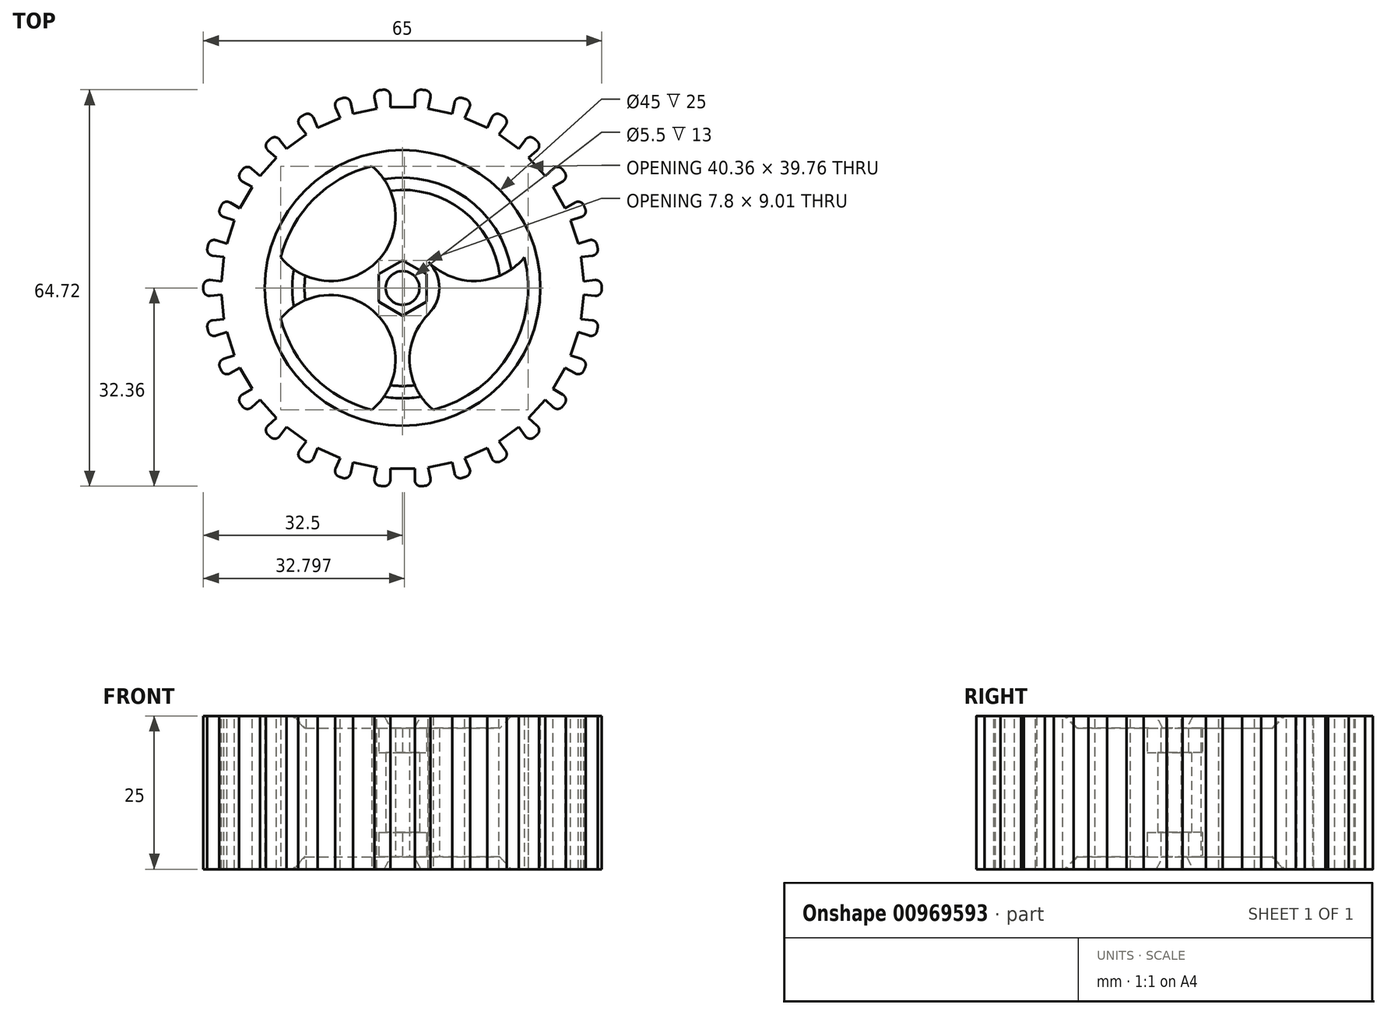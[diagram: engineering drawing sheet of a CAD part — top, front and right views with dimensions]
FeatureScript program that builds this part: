
annotation { "Feature Type Name" : "Feature", "Feature Type Description" : "" }
export const myFeature = defineFeature(function(context is Context, id is Id, definition is map)
    precondition{}
    {
        {
            var Q0;
            Q0=qCreatedBy(makeId("Top.planeOp"),FACE);
            var sketch = newSketch(context, id + "F0", { "sketchPlane" : qUnion([Q0])});
            skCircle(sketch, "E0", {"center": v(0, 0) * mm, "radius": 32.5 * mm});
            skCircle(sketch, "E1", {"center": v(0, 0) * mm, "radius": 22.5 * mm});
            skCircle(sketch, "E2", {"center": v(0, 0) * mm, "radius": 23.5 * mm});
            skCircle(sketch, "E3", {"center": v(0, 0) * mm, "radius": 20.5 * mm});
            skCircle(sketch, "E4", {"center": v(0, 0) * mm, "radius": 6 * mm});
            skArc(sketch, "E5", {"start": v(-19.88, 5) * mm, "mid": v(-4.24, 4.24) * mm, "end": v(-5, 19.88) * mm});
            skArc(sketch, "E6.MirrorCS", {"start": v(19.88, 5) * mm, "mid": v(4.24, 4.24) * mm, "end": v(5, 19.88) * mm});
            skArc(sketch, "E7.MirrorCS", {"start": v(-19.88, -5) * mm, "mid": v(-4.24, -4.24) * mm, "end": v(-5, -19.88) * mm});
            skArc(sketch, "E8.MirrorCS", {"start": v(19.88, -5) * mm, "mid": v(4.24, -4.24) * mm, "end": v(5, -19.88) * mm});
            skCircle(sketch, "E9.cCircle", {"center": v(0, 0) * mm, "radius": 3.9 * mm, "construction": true});
            skLineSegment(sketch, "E9.0", {"start": v(3.9, 2.25) * mm, "end": v(3.9, -2.25) * mm});
            skLineSegment(sketch, "E9.1", {"start": v(3.9, -2.25) * mm, "end": v(0, -4.5) * mm});
            skLineSegment(sketch, "E9.2", {"start": v(0, -4.5) * mm, "end": v(-3.9, -2.25) * mm});
            skLineSegment(sketch, "E9.3", {"start": v(-3.9, -2.25) * mm, "end": v(-3.9, 2.25) * mm});
            skLineSegment(sketch, "E9.4", {"start": v(-3.9, 2.25) * mm, "end": v(0, 4.5) * mm});
            skLineSegment(sketch, "E9.5", {"start": v(0, 4.5) * mm, "end": v(3.9, 2.25) * mm});
            skPoint(sketch, "E9.0.midPoint", {"position": v(3.9, 0) * mm});
            skCircle(sketch, "E10", {"center": v(0, 0) * mm, "radius": 3 * mm});
            skCircle(sketch, "E11", {"center": v(0, 0) * mm, "radius": 2.75 * mm});
            skSolve(sketch);
        }
        {
            var Q0;
            {var subQ0=sQuery(id+"F0.wireOp",EDGE,"E5");var subQ1=sQuery(id+"F0.wireOp",EDGE,"E3");var subQ2=makeQuery(id+"F0.imprint","INTERSECT",VERTEX,{"disambiguationData":[OD(1.0)],"derivedFrom":[subQ1,subQ0]});Q0=makeQuery(id+"F0.imprint","IMPRINT",FACE,{"disambiguationData":[TD([[makeQuery(id+"F0.imprint","IMPRINT",EDGE,{"disambiguationData":[TD([[subQ2,1.0]])],"derivedFrom":subQ1}),1.0]])]});}
            var Q1;
            {var subQ0=sQuery(id+"F0.wireOp",EDGE,"E5");var subQ1=sQuery(id+"F0.wireOp",EDGE,"E3");var subQ2=makeQuery(id+"F0.imprint","INTERSECT",VERTEX,{"disambiguationData":[OD(0.0)],"derivedFrom":[subQ1,subQ0]});Q1=makeQuery(id+"F0.imprint","IMPRINT",FACE,{"disambiguationData":[TD([[makeQuery(id+"F0.imprint","IMPRINT",EDGE,{"disambiguationData":[TD([[subQ2,-1.0]])],"derivedFrom":subQ1}),1.0]])]});}
            var Q2;
            {var subQ0=sQuery(id+"F0.wireOp",EDGE,"E7.MirrorCS");var subQ1=sQuery(id+"F0.wireOp",EDGE,"E3");var subQ2=makeQuery(id+"F0.imprint","INTERSECT",VERTEX,{"disambiguationData":[OD(1.0)],"derivedFrom":[subQ1,subQ0]});Q2=makeQuery(id+"F0.imprint","IMPRINT",FACE,{"disambiguationData":[TD([[makeQuery(id+"F0.imprint","IMPRINT",EDGE,{"disambiguationData":[TD([[subQ2,-1.0]])],"derivedFrom":subQ1}),1.0]])]});}
            var Q3;
            {var subQ0=sQuery(id+"F0.wireOp",EDGE,"E6.MirrorCS");var subQ1=sQuery(id+"F0.wireOp",EDGE,"E3");var subQ2=makeQuery(id+"F0.imprint","INTERSECT",VERTEX,{"disambiguationData":[OD(0.0)],"derivedFrom":[subQ1,subQ0]});Q3=makeQuery(id+"F0.imprint","IMPRINT",FACE,{"disambiguationData":[TD([[makeQuery(id+"F0.imprint","IMPRINT",EDGE,{"disambiguationData":[TD([[subQ2,1.0]])],"derivedFrom":subQ1}),1.0]])]});}
            var Q4;
            Q4=makeQuery(id+"F0.imprint","IMPRINT",FACE,{"disambiguationData":[TD([[makeQuery(id+"F0.imprint","IMPRINT",EDGE,{"derivedFrom":sQuery(id+"F0.wireOp",EDGE,"E1")}),1.0]])]});
            var Q5;
            Q5=makeQuery(id+"F0.imprint","IMPRINT",FACE,{"disambiguationData":[TD([[makeQuery(id+"F0.imprint","IMPRINT",EDGE,{"derivedFrom":sQuery(id+"F0.wireOp",EDGE,"E9.0")}),1.0]])]});
            var Q6;
            Q6=makeQuery(id+"F0.imprint","IMPRINT",FACE,{"disambiguationData":[TD([[makeQuery(id+"F0.imprint","IMPRINT",EDGE,{"derivedFrom":sQuery(id+"F0.wireOp",EDGE,"E9.0")}),-1.0]])]});
            extrude(context, id + "F1", {"entities" : qUnion([Q0, Q1, Q2, Q3, Q4, Q5, Q6]), "depth" : 25 * mm, "offsetDistance" : 25 * mm});
        }
        {
            var Q0;
            Q0=makeQuery(id+"F0.imprint","IMPRINT",FACE,{"disambiguationData":[TD([[makeQuery(id+"F0.imprint","IMPRINT",EDGE,{"derivedFrom":sQuery(id+"F0.wireOp",EDGE,"E0")}),1.0]])]});
            var Q1;
            Q1=makeQuery(id+"F0.imprint","IMPRINT",FACE,{"disambiguationData":[TD([[makeQuery(id+"F0.imprint","IMPRINT",EDGE,{"derivedFrom":sQuery(id+"F0.wireOp",EDGE,"E1")}),-1.0]])]});
            extrude(context, id + "F2", {"entities" : qUnion([Q0, Q1]), "depth" : 25 * mm, "offsetDistance" : 25 * mm});
        }
        {
            var Q0;
            Q0=makeQuery(id+"F0.imprint","IMPRINT",FACE,{"disambiguationData":[TD([[makeQuery(id+"F0.imprint","IMPRINT",EDGE,{"derivedFrom":sQuery(id+"F0.wireOp",EDGE,"E10")}),1.0]])]});
            extrude(context, id + "F3", {"entities" : qUnion([Q0]), "operationType" : NewBodyOperationType.ADD, "depth" : 23 * mm, "offsetDistance" : 25 * mm, "hasSecondDirection" : true, "secondDirectionOppositeDirection" : true, "secondDirectionDepth" : -2 * mm});
        }
        {
            var Q0;
            Q0=makeQuery(id+"F1.opExtrude","CAP_EDGE",EDGE,{"disambiguationData":[OSD([sQuery(id+"F0.wireOp",EDGE,"E10")])],"isStart":true});
            var Q1;
            Q1=makeQuery(id+"F1.opExtrude","CAP_EDGE",EDGE,{"disambiguationData":[OSD([sQuery(id+"F0.wireOp",EDGE,"E10")])],"isStart":false});
            chamfer(context, id + "F4", {"entities" : qUnion([Q0, Q1]), "width" : 15 * mm, "tangentPropagation" : true});
        }
        {
            var Q0;
            Q0=qCreatedBy(makeId("Front.planeOp"),FACE);
            cPlane(context, id + "F5", {"entities" : qUnion([Q0]), "cplaneType" : CPlaneType.OFFSET, "offset" : 32.5 * mm, "width" : 150 * mm, "height" : 150 * mm});
        }
        {
            var Q0;
            Q0=qCreatedBy(id+"F5.planeOp",FACE);
            var sketch = newSketch(context, id + "F6", { "sketchPlane" : qUnion([Q0])});
            skLineSegment(sketch, "E12.bottom", {"start": v(-2, 0) * mm, "end": v(2, 0) * mm});
            skLineSegment(sketch, "E12.top", {"start": v(-2, 25) * mm, "end": v(2, 25) * mm});
            skLineSegment(sketch, "E12.left", {"start": v(-2, 0) * mm, "end": v(-2, 25) * mm});
            skLineSegment(sketch, "E12.right", {"start": v(2, 0) * mm, "end": v(2, 25) * mm});
            skSolve(sketch);
        }
        {
            var Q0;
            Q0=makeQuery(id+"F6.imprint","IMPRINT",FACE,{"disambiguationData":[TD([[makeQuery(id+"F6.imprint","IMPRINT",EDGE,{"derivedFrom":sQuery(id+"F6.wireOp",EDGE,"E12.bottom")}),1.0]])]});
            extrude(context, id + "F7", {"entities" : qUnion([Q0]), "oppositeDirection" : true, "depth" : 3 * mm, "offsetDistance" : 25 * mm});
        }
        {
            var Q0;
            Q0=makeQuery(id+"F7.opExtrude","SWEPT_BODY",BODY,{"disambiguationData":[OSD([sQuery(id+"F6.wireOp",EDGE,"E12.bottom"),sQuery(id+"F6.wireOp",EDGE,"E12.top"),sQuery(id+"F6.wireOp",EDGE,"E12.left"),sQuery(id+"F6.wireOp",EDGE,"E12.right")])]});
            var Q1;
            Q1=makeQuery(id+"F3.opExtrude","CAP_EDGE",EDGE,{"disambiguationData":[OSD([sQuery(id+"F0.wireOp",EDGE,"E11")])],"isStart":false});
            circularPattern(context, id + "F8", {"operationType" : NewBodyOperationType.REMOVE, "entities" : qUnion([Q0]), "axis" : qUnion([Q1]), "angle" : 360 * degree, "instanceCount" : 30, "equalSpace" : true});
        }
        {
            var Q0;
            Q0=makeQuery(id+"F0.imprint","IMPRINT",FACE,{"disambiguationData":[TD([[makeQuery(id+"F0.imprint","IMPRINT",EDGE,{"derivedFrom":sQuery(id+"F0.wireOp",EDGE,"E10")}),1.0]])]});
            var Q1;
            Q1=makeQuery(id+"F0.imprint","IMPRINT",FACE,{"disambiguationData":[TD([[makeQuery(id+"F0.imprint","IMPRINT",EDGE,{"derivedFrom":sQuery(id+"F0.wireOp",EDGE,"E9.0")}),-1.0]])]});
            extrude(context, id + "F9", {"entities" : qUnion([Q0, Q1]), "operationType" : NewBodyOperationType.REMOVE, "depth" : 6 * mm, "offsetDistance" : 25 * mm});
        }
        {
            var Q0;
            Q0=makeQuery(id+"F0.imprint","IMPRINT",FACE,{"disambiguationData":[TD([[makeQuery(id+"F0.imprint","IMPRINT",EDGE,{"derivedFrom":sQuery(id+"F0.wireOp",EDGE,"E9.0")}),-1.0]])]});
            var Q1;
            Q1=makeQuery(id+"F0.imprint","IMPRINT",FACE,{"disambiguationData":[TD([[makeQuery(id+"F0.imprint","IMPRINT",EDGE,{"derivedFrom":sQuery(id+"F0.wireOp",EDGE,"E10")}),1.0]])]});
            extrude(context, id + "F10", {"entities" : qUnion([Q0, Q1]), "operationType" : NewBodyOperationType.REMOVE, "depth" : 25 * mm, "offsetDistance" : 25 * mm, "hasSecondDirection" : true, "secondDirectionOppositeDirection" : false, "secondDirectionDepth" : 19 * mm});
        }
        {
            var Q0;
            Q0=makeQuery(id+"F8.boolean.opBoolean","INTERSECT",EDGE,{"derivedFrom":[makeQuery(id+"F2.opExtrude","SWEPT_FACE",FACE,{"disambiguationData":[OSD([sQuery(id+"F0.wireOp",EDGE,"E0")])]}),makeQuery(id+"F8.opPattern","COPY",FACE,{"derivedFrom":makeQuery(id+"F7.opExtrude","SWEPT_FACE",FACE,{"disambiguationData":[OSD([sQuery(id+"F6.wireOp",EDGE,"E12.right")])]}),"instanceName":"17"})]});
            var Q1;
            Q1=makeQuery(id+"F8.boolean.opBoolean","INTERSECT",EDGE,{"derivedFrom":[makeQuery(id+"F2.opExtrude","SWEPT_FACE",FACE,{"disambiguationData":[OSD([sQuery(id+"F0.wireOp",EDGE,"E0")])]}),makeQuery(id+"F8.opPattern","COPY",FACE,{"derivedFrom":makeQuery(id+"F7.opExtrude","SWEPT_FACE",FACE,{"disambiguationData":[OSD([sQuery(id+"F6.wireOp",EDGE,"E12.left")])]}),"instanceName":"18"})]});
            var Q2;
            Q2=makeQuery(id+"F8.boolean.opBoolean","INTERSECT",EDGE,{"derivedFrom":[makeQuery(id+"F2.opExtrude","SWEPT_FACE",FACE,{"disambiguationData":[OSD([sQuery(id+"F0.wireOp",EDGE,"E0")])]}),makeQuery(id+"F8.opPattern","COPY",FACE,{"derivedFrom":makeQuery(id+"F7.opExtrude","SWEPT_FACE",FACE,{"disambiguationData":[OSD([sQuery(id+"F6.wireOp",EDGE,"E12.right")])]}),"instanceName":"18"})]});
            var Q3;
            Q3=makeQuery(id+"F8.boolean.opBoolean","INTERSECT",EDGE,{"derivedFrom":[makeQuery(id+"F2.opExtrude","SWEPT_FACE",FACE,{"disambiguationData":[OSD([sQuery(id+"F0.wireOp",EDGE,"E0")])]}),makeQuery(id+"F8.opPattern","COPY",FACE,{"derivedFrom":makeQuery(id+"F7.opExtrude","SWEPT_FACE",FACE,{"disambiguationData":[OSD([sQuery(id+"F6.wireOp",EDGE,"E12.left")])]}),"instanceName":"19"})]});
            var Q4;
            Q4=makeQuery(id+"F8.boolean.opBoolean","INTERSECT",EDGE,{"derivedFrom":[makeQuery(id+"F2.opExtrude","SWEPT_FACE",FACE,{"disambiguationData":[OSD([sQuery(id+"F0.wireOp",EDGE,"E0")])]}),makeQuery(id+"F8.opPattern","COPY",FACE,{"derivedFrom":makeQuery(id+"F7.opExtrude","SWEPT_FACE",FACE,{"disambiguationData":[OSD([sQuery(id+"F6.wireOp",EDGE,"E12.right")])]}),"instanceName":"19"})]});
            var Q5;
            Q5=makeQuery(id+"F8.boolean.opBoolean","INTERSECT",EDGE,{"derivedFrom":[makeQuery(id+"F2.opExtrude","SWEPT_FACE",FACE,{"disambiguationData":[OSD([sQuery(id+"F0.wireOp",EDGE,"E0")])]}),makeQuery(id+"F8.opPattern","COPY",FACE,{"derivedFrom":makeQuery(id+"F7.opExtrude","SWEPT_FACE",FACE,{"disambiguationData":[OSD([sQuery(id+"F6.wireOp",EDGE,"E12.left")])]}),"instanceName":"20"})]});
            var Q6;
            Q6=makeQuery(id+"F8.boolean.opBoolean","INTERSECT",EDGE,{"derivedFrom":[makeQuery(id+"F2.opExtrude","SWEPT_FACE",FACE,{"disambiguationData":[OSD([sQuery(id+"F0.wireOp",EDGE,"E0")])]}),makeQuery(id+"F8.opPattern","COPY",FACE,{"derivedFrom":makeQuery(id+"F7.opExtrude","SWEPT_FACE",FACE,{"disambiguationData":[OSD([sQuery(id+"F6.wireOp",EDGE,"E12.right")])]}),"instanceName":"20"})]});
            var Q7;
            Q7=makeQuery(id+"F8.boolean.opBoolean","INTERSECT",EDGE,{"derivedFrom":[makeQuery(id+"F2.opExtrude","SWEPT_FACE",FACE,{"disambiguationData":[OSD([sQuery(id+"F0.wireOp",EDGE,"E0")])]}),makeQuery(id+"F8.opPattern","COPY",FACE,{"derivedFrom":makeQuery(id+"F7.opExtrude","SWEPT_FACE",FACE,{"disambiguationData":[OSD([sQuery(id+"F6.wireOp",EDGE,"E12.left")])]}),"instanceName":"21"})]});
            var Q8;
            Q8=makeQuery(id+"F8.boolean.opBoolean","INTERSECT",EDGE,{"derivedFrom":[makeQuery(id+"F2.opExtrude","SWEPT_FACE",FACE,{"disambiguationData":[OSD([sQuery(id+"F0.wireOp",EDGE,"E0")])]}),makeQuery(id+"F8.opPattern","COPY",FACE,{"derivedFrom":makeQuery(id+"F7.opExtrude","SWEPT_FACE",FACE,{"disambiguationData":[OSD([sQuery(id+"F6.wireOp",EDGE,"E12.right")])]}),"instanceName":"21"})]});
            var Q9;
            Q9=makeQuery(id+"F8.boolean.opBoolean","INTERSECT",EDGE,{"derivedFrom":[makeQuery(id+"F2.opExtrude","SWEPT_FACE",FACE,{"disambiguationData":[OSD([sQuery(id+"F0.wireOp",EDGE,"E0")])]}),makeQuery(id+"F8.opPattern","COPY",FACE,{"derivedFrom":makeQuery(id+"F7.opExtrude","SWEPT_FACE",FACE,{"disambiguationData":[OSD([sQuery(id+"F6.wireOp",EDGE,"E12.left")])]}),"instanceName":"22"})]});
            var Q10;
            Q10=makeQuery(id+"F8.boolean.opBoolean","INTERSECT",EDGE,{"derivedFrom":[makeQuery(id+"F2.opExtrude","SWEPT_FACE",FACE,{"disambiguationData":[OSD([sQuery(id+"F0.wireOp",EDGE,"E0")])]}),makeQuery(id+"F8.opPattern","COPY",FACE,{"derivedFrom":makeQuery(id+"F7.opExtrude","SWEPT_FACE",FACE,{"disambiguationData":[OSD([sQuery(id+"F6.wireOp",EDGE,"E12.right")])]}),"instanceName":"22"})]});
            var Q11;
            Q11=makeQuery(id+"F8.boolean.opBoolean","INTERSECT",EDGE,{"derivedFrom":[makeQuery(id+"F2.opExtrude","SWEPT_FACE",FACE,{"disambiguationData":[OSD([sQuery(id+"F0.wireOp",EDGE,"E0")])]}),makeQuery(id+"F8.opPattern","COPY",FACE,{"derivedFrom":makeQuery(id+"F7.opExtrude","SWEPT_FACE",FACE,{"disambiguationData":[OSD([sQuery(id+"F6.wireOp",EDGE,"E12.left")])]}),"instanceName":"23"})]});
            var Q12;
            Q12=makeQuery(id+"F8.boolean.opBoolean","INTERSECT",EDGE,{"derivedFrom":[makeQuery(id+"F2.opExtrude","SWEPT_FACE",FACE,{"disambiguationData":[OSD([sQuery(id+"F0.wireOp",EDGE,"E0")])]}),makeQuery(id+"F8.opPattern","COPY",FACE,{"derivedFrom":makeQuery(id+"F7.opExtrude","SWEPT_FACE",FACE,{"disambiguationData":[OSD([sQuery(id+"F6.wireOp",EDGE,"E12.right")])]}),"instanceName":"23"})]});
            var Q13;
            Q13=makeQuery(id+"F8.boolean.opBoolean","INTERSECT",EDGE,{"derivedFrom":[makeQuery(id+"F2.opExtrude","SWEPT_FACE",FACE,{"disambiguationData":[OSD([sQuery(id+"F0.wireOp",EDGE,"E0")])]}),makeQuery(id+"F8.opPattern","COPY",FACE,{"derivedFrom":makeQuery(id+"F7.opExtrude","SWEPT_FACE",FACE,{"disambiguationData":[OSD([sQuery(id+"F6.wireOp",EDGE,"E12.left")])]}),"instanceName":"24"})]});
            var Q14;
            Q14=makeQuery(id+"F8.boolean.opBoolean","INTERSECT",EDGE,{"derivedFrom":[makeQuery(id+"F2.opExtrude","SWEPT_FACE",FACE,{"disambiguationData":[OSD([sQuery(id+"F0.wireOp",EDGE,"E0")])]}),makeQuery(id+"F8.opPattern","COPY",FACE,{"derivedFrom":makeQuery(id+"F7.opExtrude","SWEPT_FACE",FACE,{"disambiguationData":[OSD([sQuery(id+"F6.wireOp",EDGE,"E12.right")])]}),"instanceName":"24"})]});
            var Q15;
            Q15=makeQuery(id+"F8.boolean.opBoolean","INTERSECT",EDGE,{"derivedFrom":[makeQuery(id+"F2.opExtrude","SWEPT_FACE",FACE,{"disambiguationData":[OSD([sQuery(id+"F0.wireOp",EDGE,"E0")])]}),makeQuery(id+"F8.opPattern","COPY",FACE,{"derivedFrom":makeQuery(id+"F7.opExtrude","SWEPT_FACE",FACE,{"disambiguationData":[OSD([sQuery(id+"F6.wireOp",EDGE,"E12.left")])]}),"instanceName":"25"})]});
            var Q16;
            Q16=makeQuery(id+"F8.boolean.opBoolean","INTERSECT",EDGE,{"derivedFrom":[makeQuery(id+"F2.opExtrude","SWEPT_FACE",FACE,{"disambiguationData":[OSD([sQuery(id+"F0.wireOp",EDGE,"E0")])]}),makeQuery(id+"F8.opPattern","COPY",FACE,{"derivedFrom":makeQuery(id+"F7.opExtrude","SWEPT_FACE",FACE,{"disambiguationData":[OSD([sQuery(id+"F6.wireOp",EDGE,"E12.right")])]}),"instanceName":"25"})]});
            var Q17;
            Q17=makeQuery(id+"F8.boolean.opBoolean","INTERSECT",EDGE,{"derivedFrom":[makeQuery(id+"F2.opExtrude","SWEPT_FACE",FACE,{"disambiguationData":[OSD([sQuery(id+"F0.wireOp",EDGE,"E0")])]}),makeQuery(id+"F8.opPattern","COPY",FACE,{"derivedFrom":makeQuery(id+"F7.opExtrude","SWEPT_FACE",FACE,{"disambiguationData":[OSD([sQuery(id+"F6.wireOp",EDGE,"E12.left")])]}),"instanceName":"26"})]});
            var Q18;
            Q18=makeQuery(id+"F8.boolean.opBoolean","INTERSECT",EDGE,{"derivedFrom":[makeQuery(id+"F2.opExtrude","SWEPT_FACE",FACE,{"disambiguationData":[OSD([sQuery(id+"F0.wireOp",EDGE,"E0")])]}),makeQuery(id+"F8.opPattern","COPY",FACE,{"derivedFrom":makeQuery(id+"F7.opExtrude","SWEPT_FACE",FACE,{"disambiguationData":[OSD([sQuery(id+"F6.wireOp",EDGE,"E12.right")])]}),"instanceName":"26"})]});
            var Q19;
            Q19=makeQuery(id+"F8.boolean.opBoolean","INTERSECT",EDGE,{"derivedFrom":[makeQuery(id+"F2.opExtrude","SWEPT_FACE",FACE,{"disambiguationData":[OSD([sQuery(id+"F0.wireOp",EDGE,"E0")])]}),makeQuery(id+"F8.opPattern","COPY",FACE,{"derivedFrom":makeQuery(id+"F7.opExtrude","SWEPT_FACE",FACE,{"disambiguationData":[OSD([sQuery(id+"F6.wireOp",EDGE,"E12.left")])]}),"instanceName":"27"})]});
            var Q20;
            Q20=makeQuery(id+"F8.boolean.opBoolean","INTERSECT",EDGE,{"derivedFrom":[makeQuery(id+"F2.opExtrude","SWEPT_FACE",FACE,{"disambiguationData":[OSD([sQuery(id+"F0.wireOp",EDGE,"E0")])]}),makeQuery(id+"F8.opPattern","COPY",FACE,{"derivedFrom":makeQuery(id+"F7.opExtrude","SWEPT_FACE",FACE,{"disambiguationData":[OSD([sQuery(id+"F6.wireOp",EDGE,"E12.right")])]}),"instanceName":"27"})]});
            var Q21;
            Q21=makeQuery(id+"F8.boolean.opBoolean","INTERSECT",EDGE,{"derivedFrom":[makeQuery(id+"F2.opExtrude","SWEPT_FACE",FACE,{"disambiguationData":[OSD([sQuery(id+"F0.wireOp",EDGE,"E0")])]}),makeQuery(id+"F8.opPattern","COPY",FACE,{"derivedFrom":makeQuery(id+"F7.opExtrude","SWEPT_FACE",FACE,{"disambiguationData":[OSD([sQuery(id+"F6.wireOp",EDGE,"E12.left")])]}),"instanceName":"28"})]});
            var Q22;
            Q22=makeQuery(id+"F8.boolean.opBoolean","INTERSECT",EDGE,{"derivedFrom":[makeQuery(id+"F2.opExtrude","SWEPT_FACE",FACE,{"disambiguationData":[OSD([sQuery(id+"F0.wireOp",EDGE,"E0")])]}),makeQuery(id+"F8.opPattern","COPY",FACE,{"derivedFrom":makeQuery(id+"F7.opExtrude","SWEPT_FACE",FACE,{"disambiguationData":[OSD([sQuery(id+"F6.wireOp",EDGE,"E12.right")])]}),"instanceName":"28"})]});
            var Q23;
            Q23=makeQuery(id+"F8.boolean.opBoolean","INTERSECT",EDGE,{"derivedFrom":[makeQuery(id+"F2.opExtrude","SWEPT_FACE",FACE,{"disambiguationData":[OSD([sQuery(id+"F0.wireOp",EDGE,"E0")])]}),makeQuery(id+"F8.opPattern","COPY",FACE,{"derivedFrom":makeQuery(id+"F7.opExtrude","SWEPT_FACE",FACE,{"disambiguationData":[OSD([sQuery(id+"F6.wireOp",EDGE,"E12.left")])]}),"instanceName":"29"})]});
            var Q24;
            Q24=makeQuery(id+"F8.boolean.opBoolean","INTERSECT",EDGE,{"derivedFrom":[makeQuery(id+"F2.opExtrude","SWEPT_FACE",FACE,{"disambiguationData":[OSD([sQuery(id+"F0.wireOp",EDGE,"E0")])]}),makeQuery(id+"F8.opPattern","COPY",FACE,{"derivedFrom":makeQuery(id+"F7.opExtrude","SWEPT_FACE",FACE,{"disambiguationData":[OSD([sQuery(id+"F6.wireOp",EDGE,"E12.right")])]}),"instanceName":"29"})]});
            var Q25;
            Q25=makeQuery(id+"F8.boolean.opBoolean","INTERSECT",EDGE,{"derivedFrom":[makeQuery(id+"F2.opExtrude","SWEPT_FACE",FACE,{"disambiguationData":[OSD([sQuery(id+"F0.wireOp",EDGE,"E0")])]}),makeQuery(id+"F7.opExtrude","SWEPT_FACE",FACE,{"disambiguationData":[OSD([sQuery(id+"F6.wireOp",EDGE,"E12.left")])]})]});
            var Q26;
            Q26=makeQuery(id+"F8.boolean.opBoolean","INTERSECT",EDGE,{"derivedFrom":[makeQuery(id+"F2.opExtrude","SWEPT_FACE",FACE,{"disambiguationData":[OSD([sQuery(id+"F0.wireOp",EDGE,"E0")])]}),makeQuery(id+"F7.opExtrude","SWEPT_FACE",FACE,{"disambiguationData":[OSD([sQuery(id+"F6.wireOp",EDGE,"E12.right")])]})]});
            var Q27;
            Q27=makeQuery(id+"F8.boolean.opBoolean","INTERSECT",EDGE,{"derivedFrom":[makeQuery(id+"F2.opExtrude","SWEPT_FACE",FACE,{"disambiguationData":[OSD([sQuery(id+"F0.wireOp",EDGE,"E0")])]}),makeQuery(id+"F8.opPattern","COPY",FACE,{"derivedFrom":makeQuery(id+"F7.opExtrude","SWEPT_FACE",FACE,{"disambiguationData":[OSD([sQuery(id+"F6.wireOp",EDGE,"E12.left")])]}),"instanceName":"1"})]});
            var Q28;
            Q28=makeQuery(id+"F8.boolean.opBoolean","INTERSECT",EDGE,{"derivedFrom":[makeQuery(id+"F2.opExtrude","SWEPT_FACE",FACE,{"disambiguationData":[OSD([sQuery(id+"F0.wireOp",EDGE,"E0")])]}),makeQuery(id+"F8.opPattern","COPY",FACE,{"derivedFrom":makeQuery(id+"F7.opExtrude","SWEPT_FACE",FACE,{"disambiguationData":[OSD([sQuery(id+"F6.wireOp",EDGE,"E12.right")])]}),"instanceName":"1"})]});
            var Q29;
            Q29=makeQuery(id+"F8.boolean.opBoolean","INTERSECT",EDGE,{"derivedFrom":[makeQuery(id+"F2.opExtrude","SWEPT_FACE",FACE,{"disambiguationData":[OSD([sQuery(id+"F0.wireOp",EDGE,"E0")])]}),makeQuery(id+"F8.opPattern","COPY",FACE,{"derivedFrom":makeQuery(id+"F7.opExtrude","SWEPT_FACE",FACE,{"disambiguationData":[OSD([sQuery(id+"F6.wireOp",EDGE,"E12.left")])]}),"instanceName":"2"})]});
            var Q30;
            Q30=makeQuery(id+"F8.boolean.opBoolean","INTERSECT",EDGE,{"derivedFrom":[makeQuery(id+"F2.opExtrude","SWEPT_FACE",FACE,{"disambiguationData":[OSD([sQuery(id+"F0.wireOp",EDGE,"E0")])]}),makeQuery(id+"F8.opPattern","COPY",FACE,{"derivedFrom":makeQuery(id+"F7.opExtrude","SWEPT_FACE",FACE,{"disambiguationData":[OSD([sQuery(id+"F6.wireOp",EDGE,"E12.right")])]}),"instanceName":"2"})]});
            var Q31;
            Q31=makeQuery(id+"F8.boolean.opBoolean","INTERSECT",EDGE,{"derivedFrom":[makeQuery(id+"F2.opExtrude","SWEPT_FACE",FACE,{"disambiguationData":[OSD([sQuery(id+"F0.wireOp",EDGE,"E0")])]}),makeQuery(id+"F8.opPattern","COPY",FACE,{"derivedFrom":makeQuery(id+"F7.opExtrude","SWEPT_FACE",FACE,{"disambiguationData":[OSD([sQuery(id+"F6.wireOp",EDGE,"E12.left")])]}),"instanceName":"3"})]});
            var Q32;
            Q32=makeQuery(id+"F8.boolean.opBoolean","INTERSECT",EDGE,{"derivedFrom":[makeQuery(id+"F2.opExtrude","SWEPT_FACE",FACE,{"disambiguationData":[OSD([sQuery(id+"F0.wireOp",EDGE,"E0")])]}),makeQuery(id+"F8.opPattern","COPY",FACE,{"derivedFrom":makeQuery(id+"F7.opExtrude","SWEPT_FACE",FACE,{"disambiguationData":[OSD([sQuery(id+"F6.wireOp",EDGE,"E12.right")])]}),"instanceName":"3"})]});
            var Q33;
            Q33=makeQuery(id+"F8.boolean.opBoolean","INTERSECT",EDGE,{"derivedFrom":[makeQuery(id+"F2.opExtrude","SWEPT_FACE",FACE,{"disambiguationData":[OSD([sQuery(id+"F0.wireOp",EDGE,"E0")])]}),makeQuery(id+"F8.opPattern","COPY",FACE,{"derivedFrom":makeQuery(id+"F7.opExtrude","SWEPT_FACE",FACE,{"disambiguationData":[OSD([sQuery(id+"F6.wireOp",EDGE,"E12.left")])]}),"instanceName":"4"})]});
            var Q34;
            Q34=makeQuery(id+"F8.boolean.opBoolean","INTERSECT",EDGE,{"derivedFrom":[makeQuery(id+"F2.opExtrude","SWEPT_FACE",FACE,{"disambiguationData":[OSD([sQuery(id+"F0.wireOp",EDGE,"E0")])]}),makeQuery(id+"F8.opPattern","COPY",FACE,{"derivedFrom":makeQuery(id+"F7.opExtrude","SWEPT_FACE",FACE,{"disambiguationData":[OSD([sQuery(id+"F6.wireOp",EDGE,"E12.right")])]}),"instanceName":"4"})]});
            var Q35;
            Q35=makeQuery(id+"F8.boolean.opBoolean","INTERSECT",EDGE,{"derivedFrom":[makeQuery(id+"F2.opExtrude","SWEPT_FACE",FACE,{"disambiguationData":[OSD([sQuery(id+"F0.wireOp",EDGE,"E0")])]}),makeQuery(id+"F8.opPattern","COPY",FACE,{"derivedFrom":makeQuery(id+"F7.opExtrude","SWEPT_FACE",FACE,{"disambiguationData":[OSD([sQuery(id+"F6.wireOp",EDGE,"E12.left")])]}),"instanceName":"5"})]});
            var Q36;
            Q36=makeQuery(id+"F8.boolean.opBoolean","INTERSECT",EDGE,{"derivedFrom":[makeQuery(id+"F2.opExtrude","SWEPT_FACE",FACE,{"disambiguationData":[OSD([sQuery(id+"F0.wireOp",EDGE,"E0")])]}),makeQuery(id+"F8.opPattern","COPY",FACE,{"derivedFrom":makeQuery(id+"F7.opExtrude","SWEPT_FACE",FACE,{"disambiguationData":[OSD([sQuery(id+"F6.wireOp",EDGE,"E12.right")])]}),"instanceName":"5"})]});
            var Q37;
            Q37=makeQuery(id+"F8.boolean.opBoolean","INTERSECT",EDGE,{"derivedFrom":[makeQuery(id+"F2.opExtrude","SWEPT_FACE",FACE,{"disambiguationData":[OSD([sQuery(id+"F0.wireOp",EDGE,"E0")])]}),makeQuery(id+"F8.opPattern","COPY",FACE,{"derivedFrom":makeQuery(id+"F7.opExtrude","SWEPT_FACE",FACE,{"disambiguationData":[OSD([sQuery(id+"F6.wireOp",EDGE,"E12.left")])]}),"instanceName":"6"})]});
            var Q38;
            Q38=makeQuery(id+"F8.boolean.opBoolean","INTERSECT",EDGE,{"derivedFrom":[makeQuery(id+"F2.opExtrude","SWEPT_FACE",FACE,{"disambiguationData":[OSD([sQuery(id+"F0.wireOp",EDGE,"E0")])]}),makeQuery(id+"F8.opPattern","COPY",FACE,{"derivedFrom":makeQuery(id+"F7.opExtrude","SWEPT_FACE",FACE,{"disambiguationData":[OSD([sQuery(id+"F6.wireOp",EDGE,"E12.right")])]}),"instanceName":"6"})]});
            var Q39;
            Q39=makeQuery(id+"F8.boolean.opBoolean","INTERSECT",EDGE,{"derivedFrom":[makeQuery(id+"F2.opExtrude","SWEPT_FACE",FACE,{"disambiguationData":[OSD([sQuery(id+"F0.wireOp",EDGE,"E0")])]}),makeQuery(id+"F8.opPattern","COPY",FACE,{"derivedFrom":makeQuery(id+"F7.opExtrude","SWEPT_FACE",FACE,{"disambiguationData":[OSD([sQuery(id+"F6.wireOp",EDGE,"E12.left")])]}),"instanceName":"7"})]});
            var Q40;
            Q40=makeQuery(id+"F8.boolean.opBoolean","INTERSECT",EDGE,{"derivedFrom":[makeQuery(id+"F2.opExtrude","SWEPT_FACE",FACE,{"disambiguationData":[OSD([sQuery(id+"F0.wireOp",EDGE,"E0")])]}),makeQuery(id+"F8.opPattern","COPY",FACE,{"derivedFrom":makeQuery(id+"F7.opExtrude","SWEPT_FACE",FACE,{"disambiguationData":[OSD([sQuery(id+"F6.wireOp",EDGE,"E12.right")])]}),"instanceName":"7"})]});
            var Q41;
            Q41=makeQuery(id+"F8.boolean.opBoolean","INTERSECT",EDGE,{"derivedFrom":[makeQuery(id+"F2.opExtrude","SWEPT_FACE",FACE,{"disambiguationData":[OSD([sQuery(id+"F0.wireOp",EDGE,"E0")])]}),makeQuery(id+"F8.opPattern","COPY",FACE,{"derivedFrom":makeQuery(id+"F7.opExtrude","SWEPT_FACE",FACE,{"disambiguationData":[OSD([sQuery(id+"F6.wireOp",EDGE,"E12.left")])]}),"instanceName":"8"})]});
            var Q42;
            Q42=makeQuery(id+"F8.boolean.opBoolean","INTERSECT",EDGE,{"derivedFrom":[makeQuery(id+"F2.opExtrude","SWEPT_FACE",FACE,{"disambiguationData":[OSD([sQuery(id+"F0.wireOp",EDGE,"E0")])]}),makeQuery(id+"F8.opPattern","COPY",FACE,{"derivedFrom":makeQuery(id+"F7.opExtrude","SWEPT_FACE",FACE,{"disambiguationData":[OSD([sQuery(id+"F6.wireOp",EDGE,"E12.right")])]}),"instanceName":"8"})]});
            var Q43;
            Q43=makeQuery(id+"F8.boolean.opBoolean","INTERSECT",EDGE,{"derivedFrom":[makeQuery(id+"F2.opExtrude","SWEPT_FACE",FACE,{"disambiguationData":[OSD([sQuery(id+"F0.wireOp",EDGE,"E0")])]}),makeQuery(id+"F8.opPattern","COPY",FACE,{"derivedFrom":makeQuery(id+"F7.opExtrude","SWEPT_FACE",FACE,{"disambiguationData":[OSD([sQuery(id+"F6.wireOp",EDGE,"E12.left")])]}),"instanceName":"9"})]});
            var Q44;
            Q44=makeQuery(id+"F8.boolean.opBoolean","INTERSECT",EDGE,{"derivedFrom":[makeQuery(id+"F2.opExtrude","SWEPT_FACE",FACE,{"disambiguationData":[OSD([sQuery(id+"F0.wireOp",EDGE,"E0")])]}),makeQuery(id+"F8.opPattern","COPY",FACE,{"derivedFrom":makeQuery(id+"F7.opExtrude","SWEPT_FACE",FACE,{"disambiguationData":[OSD([sQuery(id+"F6.wireOp",EDGE,"E12.right")])]}),"instanceName":"9"})]});
            var Q45;
            Q45=makeQuery(id+"F8.boolean.opBoolean","INTERSECT",EDGE,{"derivedFrom":[makeQuery(id+"F2.opExtrude","SWEPT_FACE",FACE,{"disambiguationData":[OSD([sQuery(id+"F0.wireOp",EDGE,"E0")])]}),makeQuery(id+"F8.opPattern","COPY",FACE,{"derivedFrom":makeQuery(id+"F7.opExtrude","SWEPT_FACE",FACE,{"disambiguationData":[OSD([sQuery(id+"F6.wireOp",EDGE,"E12.left")])]}),"instanceName":"10"})]});
            var Q46;
            Q46=makeQuery(id+"F8.boolean.opBoolean","INTERSECT",EDGE,{"derivedFrom":[makeQuery(id+"F2.opExtrude","SWEPT_FACE",FACE,{"disambiguationData":[OSD([sQuery(id+"F0.wireOp",EDGE,"E0")])]}),makeQuery(id+"F8.opPattern","COPY",FACE,{"derivedFrom":makeQuery(id+"F7.opExtrude","SWEPT_FACE",FACE,{"disambiguationData":[OSD([sQuery(id+"F6.wireOp",EDGE,"E12.right")])]}),"instanceName":"10"})]});
            var Q47;
            Q47=makeQuery(id+"F8.boolean.opBoolean","INTERSECT",EDGE,{"derivedFrom":[makeQuery(id+"F2.opExtrude","SWEPT_FACE",FACE,{"disambiguationData":[OSD([sQuery(id+"F0.wireOp",EDGE,"E0")])]}),makeQuery(id+"F8.opPattern","COPY",FACE,{"derivedFrom":makeQuery(id+"F7.opExtrude","SWEPT_FACE",FACE,{"disambiguationData":[OSD([sQuery(id+"F6.wireOp",EDGE,"E12.left")])]}),"instanceName":"11"})]});
            var Q48;
            Q48=makeQuery(id+"F8.boolean.opBoolean","INTERSECT",EDGE,{"derivedFrom":[makeQuery(id+"F2.opExtrude","SWEPT_FACE",FACE,{"disambiguationData":[OSD([sQuery(id+"F0.wireOp",EDGE,"E0")])]}),makeQuery(id+"F8.opPattern","COPY",FACE,{"derivedFrom":makeQuery(id+"F7.opExtrude","SWEPT_FACE",FACE,{"disambiguationData":[OSD([sQuery(id+"F6.wireOp",EDGE,"E12.right")])]}),"instanceName":"11"})]});
            var Q49;
            Q49=makeQuery(id+"F8.boolean.opBoolean","INTERSECT",EDGE,{"derivedFrom":[makeQuery(id+"F2.opExtrude","SWEPT_FACE",FACE,{"disambiguationData":[OSD([sQuery(id+"F0.wireOp",EDGE,"E0")])]}),makeQuery(id+"F8.opPattern","COPY",FACE,{"derivedFrom":makeQuery(id+"F7.opExtrude","SWEPT_FACE",FACE,{"disambiguationData":[OSD([sQuery(id+"F6.wireOp",EDGE,"E12.left")])]}),"instanceName":"12"})]});
            var Q50;
            Q50=makeQuery(id+"F8.boolean.opBoolean","INTERSECT",EDGE,{"derivedFrom":[makeQuery(id+"F2.opExtrude","SWEPT_FACE",FACE,{"disambiguationData":[OSD([sQuery(id+"F0.wireOp",EDGE,"E0")])]}),makeQuery(id+"F8.opPattern","COPY",FACE,{"derivedFrom":makeQuery(id+"F7.opExtrude","SWEPT_FACE",FACE,{"disambiguationData":[OSD([sQuery(id+"F6.wireOp",EDGE,"E12.right")])]}),"instanceName":"12"})]});
            var Q51;
            Q51=makeQuery(id+"F8.boolean.opBoolean","INTERSECT",EDGE,{"derivedFrom":[makeQuery(id+"F2.opExtrude","SWEPT_FACE",FACE,{"disambiguationData":[OSD([sQuery(id+"F0.wireOp",EDGE,"E0")])]}),makeQuery(id+"F8.opPattern","COPY",FACE,{"derivedFrom":makeQuery(id+"F7.opExtrude","SWEPT_FACE",FACE,{"disambiguationData":[OSD([sQuery(id+"F6.wireOp",EDGE,"E12.left")])]}),"instanceName":"13"})]});
            var Q52;
            Q52=makeQuery(id+"F8.boolean.opBoolean","INTERSECT",EDGE,{"derivedFrom":[makeQuery(id+"F2.opExtrude","SWEPT_FACE",FACE,{"disambiguationData":[OSD([sQuery(id+"F0.wireOp",EDGE,"E0")])]}),makeQuery(id+"F8.opPattern","COPY",FACE,{"derivedFrom":makeQuery(id+"F7.opExtrude","SWEPT_FACE",FACE,{"disambiguationData":[OSD([sQuery(id+"F6.wireOp",EDGE,"E12.left")])]}),"instanceName":"17"})]});
            var Q53;
            Q53=makeQuery(id+"F8.boolean.opBoolean","INTERSECT",EDGE,{"derivedFrom":[makeQuery(id+"F2.opExtrude","SWEPT_FACE",FACE,{"disambiguationData":[OSD([sQuery(id+"F0.wireOp",EDGE,"E0")])]}),makeQuery(id+"F8.opPattern","COPY",FACE,{"derivedFrom":makeQuery(id+"F7.opExtrude","SWEPT_FACE",FACE,{"disambiguationData":[OSD([sQuery(id+"F6.wireOp",EDGE,"E12.right")])]}),"instanceName":"16"})]});
            var Q54;
            Q54=makeQuery(id+"F8.boolean.opBoolean","INTERSECT",EDGE,{"derivedFrom":[makeQuery(id+"F2.opExtrude","SWEPT_FACE",FACE,{"disambiguationData":[OSD([sQuery(id+"F0.wireOp",EDGE,"E0")])]}),makeQuery(id+"F8.opPattern","COPY",FACE,{"derivedFrom":makeQuery(id+"F7.opExtrude","SWEPT_FACE",FACE,{"disambiguationData":[OSD([sQuery(id+"F6.wireOp",EDGE,"E12.left")])]}),"instanceName":"16"})]});
            var Q55;
            Q55=makeQuery(id+"F8.boolean.opBoolean","INTERSECT",EDGE,{"derivedFrom":[makeQuery(id+"F2.opExtrude","SWEPT_FACE",FACE,{"disambiguationData":[OSD([sQuery(id+"F0.wireOp",EDGE,"E0")])]}),makeQuery(id+"F8.opPattern","COPY",FACE,{"derivedFrom":makeQuery(id+"F7.opExtrude","SWEPT_FACE",FACE,{"disambiguationData":[OSD([sQuery(id+"F6.wireOp",EDGE,"E12.right")])]}),"instanceName":"15"})]});
            var Q56;
            Q56=makeQuery(id+"F8.boolean.opBoolean","INTERSECT",EDGE,{"derivedFrom":[makeQuery(id+"F2.opExtrude","SWEPT_FACE",FACE,{"disambiguationData":[OSD([sQuery(id+"F0.wireOp",EDGE,"E0")])]}),makeQuery(id+"F8.opPattern","COPY",FACE,{"derivedFrom":makeQuery(id+"F7.opExtrude","SWEPT_FACE",FACE,{"disambiguationData":[OSD([sQuery(id+"F6.wireOp",EDGE,"E12.left")])]}),"instanceName":"15"})]});
            var Q57;
            Q57=makeQuery(id+"F8.boolean.opBoolean","INTERSECT",EDGE,{"derivedFrom":[makeQuery(id+"F2.opExtrude","SWEPT_FACE",FACE,{"disambiguationData":[OSD([sQuery(id+"F0.wireOp",EDGE,"E0")])]}),makeQuery(id+"F8.opPattern","COPY",FACE,{"derivedFrom":makeQuery(id+"F7.opExtrude","SWEPT_FACE",FACE,{"disambiguationData":[OSD([sQuery(id+"F6.wireOp",EDGE,"E12.right")])]}),"instanceName":"14"})]});
            var Q58;
            Q58=makeQuery(id+"F8.boolean.opBoolean","INTERSECT",EDGE,{"derivedFrom":[makeQuery(id+"F2.opExtrude","SWEPT_FACE",FACE,{"disambiguationData":[OSD([sQuery(id+"F0.wireOp",EDGE,"E0")])]}),makeQuery(id+"F8.opPattern","COPY",FACE,{"derivedFrom":makeQuery(id+"F7.opExtrude","SWEPT_FACE",FACE,{"disambiguationData":[OSD([sQuery(id+"F6.wireOp",EDGE,"E12.left")])]}),"instanceName":"14"})]});
            var Q59;
            Q59=makeQuery(id+"F8.boolean.opBoolean","INTERSECT",EDGE,{"derivedFrom":[makeQuery(id+"F2.opExtrude","SWEPT_FACE",FACE,{"disambiguationData":[OSD([sQuery(id+"F0.wireOp",EDGE,"E0")])]}),makeQuery(id+"F8.opPattern","COPY",FACE,{"derivedFrom":makeQuery(id+"F7.opExtrude","SWEPT_FACE",FACE,{"disambiguationData":[OSD([sQuery(id+"F6.wireOp",EDGE,"E12.right")])]}),"instanceName":"13"})]});
            fillet(context, id + "F11", {"entities" : qUnion([Q0, Q1, Q2, Q3, Q4, Q5, Q6, Q7, Q8, Q9, Q10, Q11, Q12, Q13, Q14, Q15, Q16, Q17, Q18, Q19, Q20, Q21, Q22, Q23, Q24, Q25, Q26, Q27, Q28, Q29, Q30, Q31, Q32, Q33, Q34, Q35, Q36, Q37, Q38, Q39, Q40, Q41, Q42, Q43, Q44, Q45, Q46, Q47, Q48, Q49, Q50, Q51, Q52, Q53, Q54, Q55, Q56, Q57, Q58, Q59]), "radius" : 1 * mm, "tangentPropagation" : true, "allowEdgeOverflow" : false});
        }
    });
